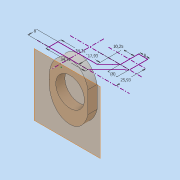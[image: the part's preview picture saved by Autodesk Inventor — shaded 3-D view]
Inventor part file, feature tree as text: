
AUTODESK INVENTOR PART (.ipt)
format: ipt  version: 2019 (Build 230136000, 136)  size: 352,256 bytes
history: native  units: mm
features: other x8, extrude x4, sketch x1
ambient origin geometry x8: Origin, YZ Plane, XZ Plane, XY Plane, X Axis, Y Axis, Z Axis, Center Point
bodies: Body1 (feature_tree), Body2 (feature_tree)
feature tree (13):
  other  "Твердое тело1"
  other  "Основной эскиз"
  extrude  "ВыдавливаниеОсновной"  Depth=34.31mm
  other  "РабПлоскость18"
  other  "РабПлоскость41"
  other  "Ручка"
  extrude  "Выдавливание32"  Depth=8.0mm
  extrude  "Корпус элипса"  Depth=34.31mm
  extrude  "Дырки"  Depth=8.0mm
  other  "Отвертстия"
  other  "Твердое тело18"
  other  "Твердое тело24"
  sketch  "Эскиз42"
